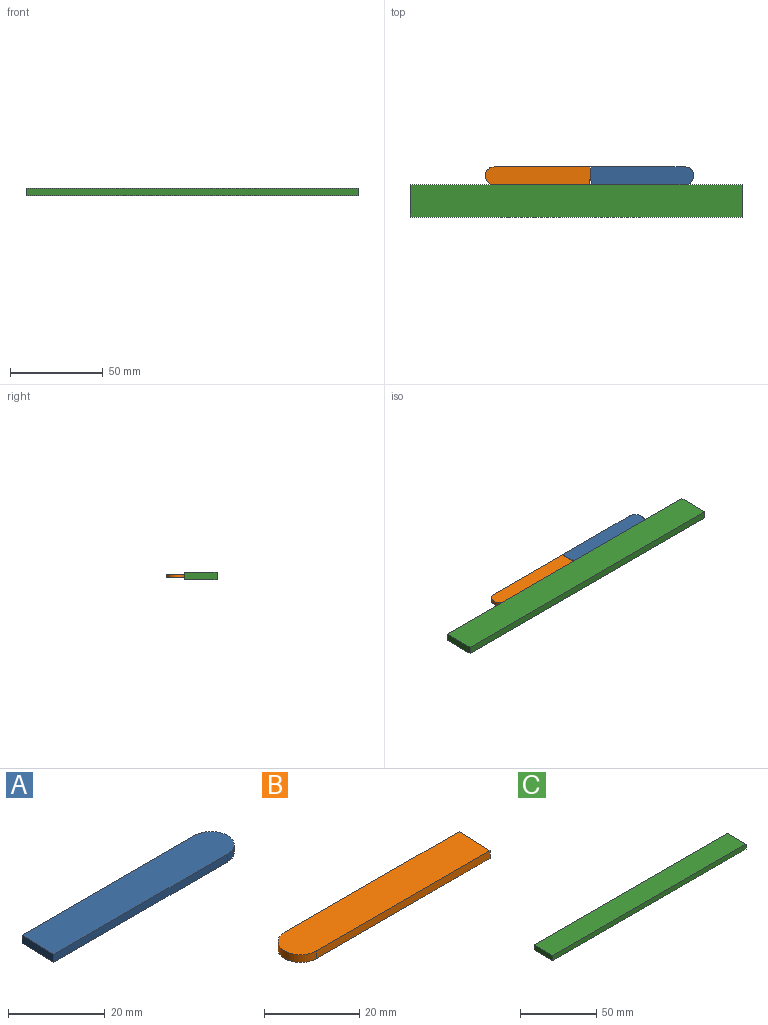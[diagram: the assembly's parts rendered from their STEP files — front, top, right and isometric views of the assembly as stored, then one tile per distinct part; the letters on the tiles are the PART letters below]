
ASSEMBLY  parts=3 mates=2
PART A: 6 faces, bbox 55.7x9.5x2 mm
  f0: plane 9.53x2mm, normal (-1,0.03,0), area 19.1mm2, adj f1,f3,f4,f5
  f1: plane 50.96x2mm, normal (0,-1,0), area 101.9mm2, adj f0,f2,f4,f5
  f2: cylinder r=4.76mm len=9.53mm, axis (0,0,-1), area 29.9mm2, adj f1,f3,f4,f5
  f3: plane 50.63x2mm, normal (0,1,0), area 101.3mm2, adj f0,f2,f4,f5
  f4: plane 55.72x9.53mm, normal (0,0,1), area 519.4mm2, adj f0,f1,f2,f3
  f5: plane 55.72x9.53mm, normal (0,0,-1), area 519.4mm2, adj f0,f1,f2,f3
PART B: 6 faces, bbox 56.7x9.5x2 mm
  f0: cylinder r=4.76mm len=9.53mm, axis (0,0,-1), area 29.9mm2, adj f1,f3,f4,f5
  f1: plane 51.59x2mm, normal (0,-1,0), area 103.2mm2, adj f0,f2,f4,f5
  f2: plane 9.53x2mm, normal (1,-0.03,0), area 19.1mm2, adj f1,f3,f4,f5
  f3: plane 51.93x2mm, normal (0,1,0), area 103.9mm2, adj f0,f2,f4,f5
  f4: plane 56.69x9.53mm, normal (0,0,1), area 528.6mm2, adj f0,f1,f2,f3
  f5: plane 56.69x9.53mm, normal (0,0,-1), area 528.6mm2, adj f0,f1,f2,f3
PART C: 6 faces, bbox 179x17.5x4 mm
  f0: plane 178.95x4mm, normal (0,1,0), area 715.8mm2, adj f1,f3,f4,f5
  f1: plane 17.46x4mm, normal (-1,0,0), area 69.8mm2, adj f0,f2,f4,f5
  f2: plane 178.95x4mm, normal (0,-1,0), area 715.8mm2, adj f1,f3,f4,f5
  f3: plane 17.46x4mm, normal (1,0,0), area 69.8mm2, adj f0,f2,f4,f5
  f4: plane 178.95x17.46mm, normal (0,0,1), area 3125mm2, adj f0,f1,f2,f3
  f5: plane 178.95x17.46mm, normal (0,0,-1), area 3125mm2, adj f0,f1,f2,f3
PLACE A rot(axis=(1,0,0),180deg) t=(-1.02,-646.02,2)mm
PLACE B t=(-0.76,0,0)mm
PLACE C at identity fixed
MATE fastened C.f0 <-> A.f3  axis (0,1,0) through (-373.89,-327.77,1)mm
MATE fastened B.f1 <-> C.f0  axis (0,-1,0) through (-425.72,-327.77,1)mm
